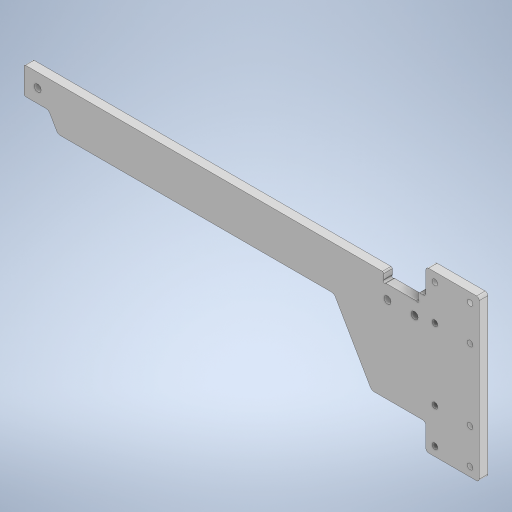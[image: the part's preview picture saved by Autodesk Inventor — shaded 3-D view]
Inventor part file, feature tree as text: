
AUTODESK INVENTOR PART (.ipt)
format: ipt  version: 2024 (Build 280153000, 153)  size: 500,224 bytes
history: native  units: mm
features: sketch x6, projected_geometry x5, extrude x4, fillet x4, hole x3, other x3
ambient origin geometry x8: Origin, YZ Plane, XZ Plane, XY Plane, X Axis, Y Axis, Z Axis, Center Point
bodies: Solid1 (feature_tree)
feature tree (25):
  sketch  "Sketch1"  dims[d1=140.0mm d2=61.4mm]
  extrude  "Extrusion1"  Depth=61.4mm
  extrude  "Extrusion2"  Depth=39.4mm
  hole  "Hole1"  [1 undecoded]
  other  "Z POSITIONING"
  other  "PRINTBED PLANE"
  other  "Y POSITIONING"
  hole  "Hole2"  [1 undecoded]
  extrude  "Extrusion3"  Depth=6.35mm
  hole  "Hole3"  [1 undecoded]
  sketch  "Sketch9"  dims[d12=6.35mm d13=0.0mm d25=18.0mm]
  fillet  "Fillet3"  Radius=35.0mm
  fillet  "Fillet4"  Radius=8.0mm
  fillet  "Fillet5"  Radius=34.15mm
  extrude  "Extrusion6"  Depth=6.35mm
  fillet  "Fillet6"  Radius=13.0mm
  sketch  "Sketch2"  dims[d3=39.4mm d4=26.0mm]
  projected_geometry  "Projected Loop1"
  projected_geometry  "Projected Loop2"
  projected_geometry  "Projected Loop3"
  sketch  "Sketch5"  dims[d5=26.0mm d6=20.0mm]
  sketch  "Sketch6"  dims[d8=316.0mm d11=25.0mm]
  projected_geometry  "Projected Loop6"
  sketch  "Sketch10"  dims[d29=10.0mm d30=0.0mm d31=4.2mm d32=6.0mm d33=4.0mm d34=2.0mm d35=90.0deg d36=8.0mm d37=20.594885mm d39=6.35mm d42=35.0mm d43=8.0mm d44=34.15mm d45=6.35mm d46=13.0mm d48=6.35mm d49=13.0mm d50=100.0mm d51=3.175mm d52=46.7mm d53=34.15mm d54=34.15mm d55=30.0mm d58=286.0mm d60=9.0mm d61=10.0mm d62=12.0mm d63=38.0mm d64=9.0mm d65=30.0mm d66=8.0mm d67=15.0mm d68=19.15mm d69=5.2mm d70=6.0mm d71=4.0mm d72=2.0mm d73=90.0deg d74=8.0mm d75=20.594885mm d78=40.0mm d79=25.5mm d81=0.0mm d82=0.0mm d83=40.0mm d84=20.0mm d85=6.35mm d86=1.75mm d87=0.5mm d88=0.5mm d89=0.5mm d90=20.0mm d91=5.3mm d92=6.0mm d93=4.0mm d94=2.0mm d95=90.0deg d96=8.0mm d97=20.594885mm d123=1.0mm d124=19.0mm d125=19.0mm d126=6.7mm d128=6.7mm d129=3.0mm d130=2.0mm d132=30.0mm d133=5.0mm d134=2.5mm d135=5.0mm d136=0.0mm d137=0.0mm d138=1.0mm d139=120.0deg d140=12.0mm d76=1.0mm d77=1.0mm d80=0.25mm]
  projected_geometry  "Projected Loop7"
note: 3 required parameter values undecoded (feature->parameter linkage not recoverable at this tier; creation-order binding heuristic only, values carry confidence <= 0.55)
